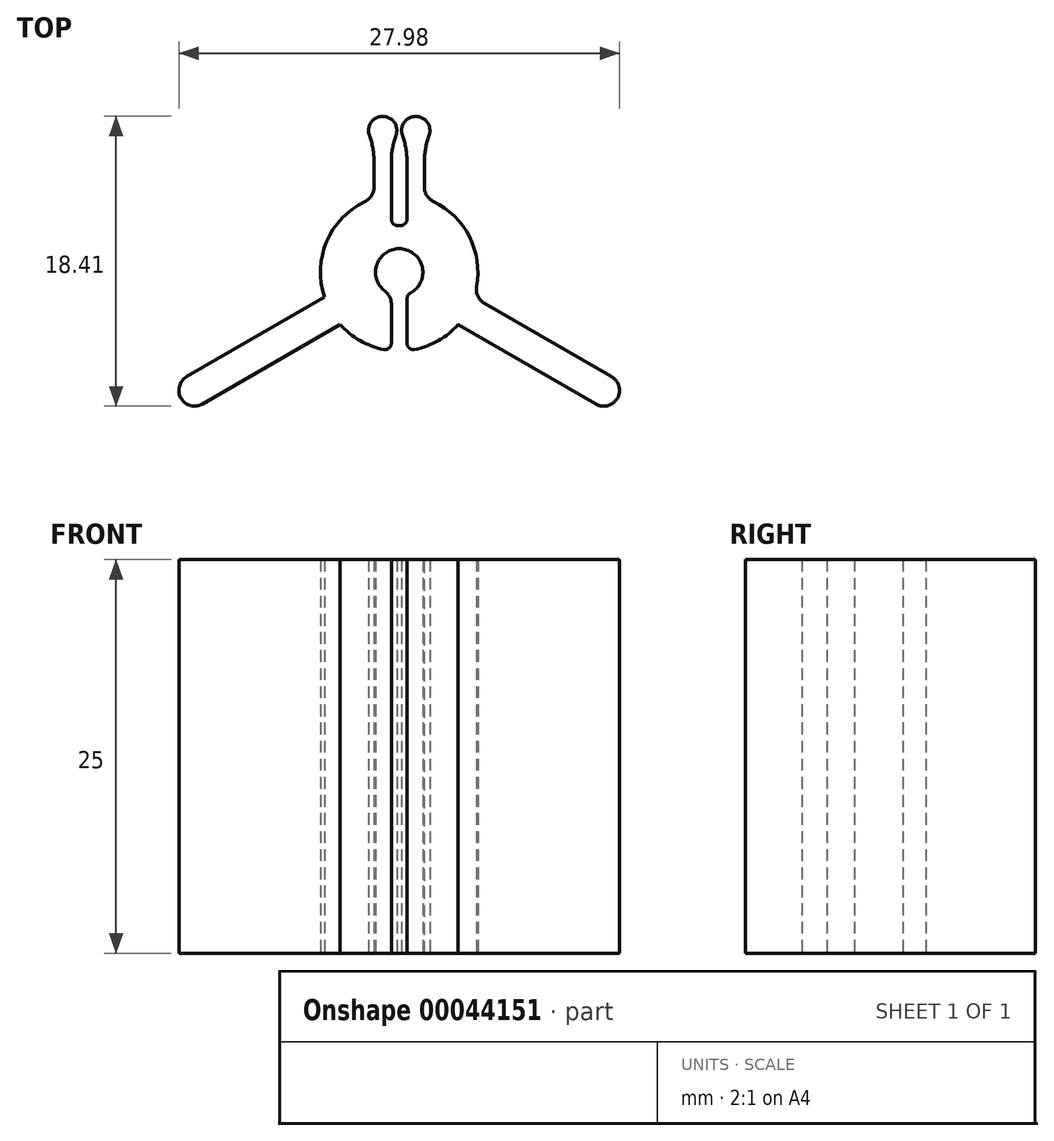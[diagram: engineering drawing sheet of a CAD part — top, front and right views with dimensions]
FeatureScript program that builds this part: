
annotation { "Feature Type Name" : "Feature", "Feature Type Description" : "" }
export const myFeature = defineFeature(function(context is Context, id is Id, definition is map)
    precondition{}
    {
        {
            var Q0;
            Q0=qCreatedBy(makeId("Top.planeOp"),FACE);
            var sketch = newSketch(context, id + "F0", { "sketchPlane" : qUnion([Q0])});
            skArc(sketch, "E0", {"start": v(-3.74, -3.32) * mm, "mid": v(-2.28, -4.45) * mm, "end": v(-0.5, -4.97) * mm});
            skArc(sketch, "E1", {"start": v(-0.5, 1.41) * mm, "mid": v(-1.5, 0) * mm, "end": v(-0.5, -1.41) * mm});
            skLineSegment(sketch, "E2", {"start": v(0, 0) * mm, "end": v(-44.7, -25.81) * mm, "construction": true});
            skLineSegment(sketch, "E3", {"start": v(0, 0) * mm, "end": v(14.9, -25.81) * mm, "construction": true});
            skLineSegment(sketch, "E4", {"start": v(-4.74, -1.58) * mm, "end": v(-13.5, -6.63) * mm});
            skLineSegment(sketch, "E5.MirrorCS", {"start": v(-3.74, -3.32) * mm, "end": v(-12.5, -8.37) * mm});
            skArc(sketch, "E6", {"start": v(-13.5, -6.63) * mm, "mid": v(-13.86, -8) * mm, "end": v(-12.5, -8.37) * mm});
            skPoint(sketch, "E7.orphan", {"position": v(-5.84, -2.21) * mm});
            skPoint(sketch, "E8.orphan", {"position": v(-4.84, -3.95) * mm});
            skLineSegment(sketch, "E9.MirrorCS", {"start": v(3.74, -3.32) * mm, "end": v(12.5, -8.37) * mm});
            skArc(sketch, "E10.MirrorCS", {"start": v(13.5, -6.63) * mm, "mid": v(13.86, -8) * mm, "end": v(12.5, -8.37) * mm});
            skLineSegment(sketch, "E11.MirrorCS", {"start": v(4.74, -1.58) * mm, "end": v(13.5, -6.63) * mm});
            skArc(sketch, "E12.trimOffspring", {"start": v(4.74, -1.58) * mm, "mid": v(4.48, 2.23) * mm, "end": v(1.6, 4.74) * mm});
            skLineSegment(sketch, "E13.MirrorCS", {"start": v(0.5, -4.97) * mm, "end": v(0.5, -1.41) * mm});
            skLineSegment(sketch, "E14.MirrorCS", {"start": v(-0.5, -4.97) * mm, "end": v(-0.5, -1.41) * mm});
            skArc(sketch, "E15.MirrorCS", {"start": v(-0.5, -1.41) * mm, "mid": v(0, 1.5) * mm, "end": v(0.5, -1.41) * mm});
            skArc(sketch, "E16.MirrorCS", {"start": v(-3.74, 3.32) * mm, "mid": v(-2.76, 4.17) * mm, "end": v(-1.6, 4.74) * mm});
            skArc(sketch, "E17.trimOffspring", {"start": v(0.5, -1.41) * mm, "mid": v(1.5, 0) * mm, "end": v(0.5, 1.41) * mm});
            skArc(sketch, "E18.trimOffspring", {"start": v(0.5, -4.97) * mm, "mid": v(2.28, -4.45) * mm, "end": v(3.74, -3.32) * mm});
            skLineSegment(sketch, "E19", {"start": v(-0.5, 4.37) * mm, "end": v(-0.5, 2.97) * mm});
            skLineSegment(sketch, "E20", {"start": v(-0.5, 2.97) * mm, "end": v(0, 2.97) * mm});
            skLineSegment(sketch, "E21.MirrorCS", {"start": v(0.5, 4.37) * mm, "end": v(0.5, 2.97) * mm});
            skLineSegment(sketch, "E22.MirrorCS", {"start": v(0.5, 2.97) * mm, "end": v(0, 2.97) * mm});
            skArc(sketch, "E23.trimOffspring", {"start": v(-3.74, 3.32) * mm, "mid": v(-4.9, 1) * mm, "end": v(-4.74, -1.58) * mm});
            skPoint(sketch, "E24.orphan", {"position": v(3.74, 3.32) * mm});
            skLineSegment(sketch, "E25", {"start": v(-1.6, 4.74) * mm, "end": v(-1.6, 8.3) * mm});
            skLineSegment(sketch, "E26", {"start": v(-0.5, 4.37) * mm, "end": v(-0.5, 8.3) * mm});
            skLineSegment(sketch, "E27.MirrorCS", {"start": v(0.5, 4.37) * mm, "end": v(0.5, 8.3) * mm});
            skLineSegment(sketch, "E28.MirrorCS", {"start": v(1.6, 4.74) * mm, "end": v(1.6, 8.3) * mm});
            skArc(sketch, "E29", {"start": v(-0.5, 8.3) * mm, "mid": v(-1.05, 9.9) * mm, "end": v(-1.6, 8.3) * mm});
            skPoint(sketch, "E30.orphan", {"position": v(-0.5, 9) * mm});
            skPoint(sketch, "E31.orphan", {"position": v(-1.6, 9) * mm});
            skArc(sketch, "E32.MirrorC", {"start": v(0.5, 8.3) * mm, "mid": v(1.05, 9.9) * mm, "end": v(1.6, 8.3) * mm});
            skPoint(sketch, "E33.orphan", {"position": v(0.5, 9) * mm});
            skPoint(sketch, "E34.MirrorCS.start.orphan", {"position": v(1.6, 9) * mm});
            skPoint(sketch, "E35.trimOffspring.end.orphan", {"position": v(0.5, 4.97) * mm});
            skPoint(sketch, "E36.trimOffspring.start.orphan", {"position": v(-0.5, 4.97) * mm});
            skSolve(sketch);
        }
        {
            var Q0;
            Q0 = qSketchRegion(id + "F0", true);
            extrude(context, id + "F1", {"entities" : qUnion([Q0]), "depth" : 25 * mm, "offsetDistance" : 25 * mm});
        }
        {
            var Q0;
            Q0=makeQuery(id+"F1.opExtrude","SWEPT_EDGE",EDGE,{"disambiguationData":[OSD([sQuery(id+"F0.wireOp",EDGE,"3mzkk0lv-jN8c-HgQ4-SjRx-xyB0a0JVrphj"),sQuery(id+"F0.wireOp",EDGE,"E36.trimOffspring")])]});
            var Q1;
            Q1=makeQuery(id+"F1.opExtrude","SWEPT_EDGE",EDGE,{"disambiguationData":[OSD([sQuery(id+"F0.wireOp",EDGE,"E12.trimOffspring"),sQuery(id+"F0.wireOp",EDGE,"587d526e-da83-4a6c-8857-2415be24daab0.MirrorCS")])]});
            var Q2;
            Q2=makeQuery(id+"F1.opExtrude","SWEPT_EDGE",EDGE,{"disambiguationData":[OSD([sQuery(id+"F0.wireOp",EDGE,"E1"),sQuery(id+"F0.wireOp",EDGE,"3mzkk0lv-jN8c-HgQ4-SjRx-xyB0a0JVrphj")])]});
            var Q3;
            Q3=makeQuery(id+"F1.opExtrude","SWEPT_EDGE",EDGE,{"disambiguationData":[OSD([sQuery(id+"F0.wireOp",EDGE,"E1"),sQuery(id+"F0.wireOp",EDGE,"587d526e-da83-4a6c-8857-2415be24daab0.MirrorCS")])]});
            var Q4;
            Q4=makeQuery(id+"F1.opExtrude","SWEPT_EDGE",EDGE,{"disambiguationData":[OSD([sQuery(id+"F0.wireOp",EDGE,"E16.MirrorCS"),sQuery(id+"F0.wireOp",EDGE,"E25")])]});
            fillet(context, id + "F2", {"entities" : qUnion([Q0, Q1, Q2, Q3, Q4]), "radius" : 1 * mm, "tangentPropagation" : true, "allowEdgeOverflow" : false});
        }
        {
            var Q0;
            Q0=makeQuery(id+"F1.opExtrude","SWEPT_EDGE",EDGE,{"disambiguationData":[OSD([sQuery(id+"F0.wireOp",EDGE,"E19"),sQuery(id+"F0.wireOp",EDGE,"E20")])]});
            var Q1;
            Q1=makeQuery(id+"F1.opExtrude","SWEPT_EDGE",EDGE,{"disambiguationData":[OSD([sQuery(id+"F0.wireOp",EDGE,"E21.MirrorCS"),sQuery(id+"F0.wireOp",EDGE,"E22.MirrorCS")])]});
            var Q2;
            Q2=makeQuery(id+"F1.opExtrude","SWEPT_EDGE",EDGE,{"disambiguationData":[OSD([sQuery(id+"F0.wireOp",EDGE,"E21.MirrorCS"),sQuery(id+"F0.wireOp",EDGE,"d01798ca-214c-46cb-be73-290c21217de8.trimOffspring")])]});
            var Q3;
            Q3=makeQuery(id+"F1.opExtrude","SWEPT_EDGE",EDGE,{"disambiguationData":[OSD([sQuery(id+"F0.wireOp",EDGE,"E16.MirrorCS"),sQuery(id+"F0.wireOp",EDGE,"E19")])]});
            var Q4;
            Q4=makeQuery(id+"F1.opExtrude","SWEPT_EDGE",EDGE,{"disambiguationData":[OSD([sQuery(id+"F0.wireOp",EDGE,"E13.MirrorCS"),sQuery(id+"F0.wireOp",EDGE,"E17.trimOffspring")])]});
            var Q5;
            Q5=makeQuery(id+"F1.opExtrude","SWEPT_EDGE",EDGE,{"disambiguationData":[OSD([sQuery(id+"F0.wireOp",EDGE,"E14.MirrorCS"),sQuery(id+"F0.wireOp",EDGE,"E15.MirrorCS")])]});
            var Q6;
            Q6=makeQuery(id+"F1.opExtrude","SWEPT_EDGE",EDGE,{"disambiguationData":[OSD([sQuery(id+"F0.wireOp",EDGE,"E13.MirrorCS"),sQuery(id+"F0.wireOp",EDGE,"E18.trimOffspring")])]});
            var Q7;
            Q7=makeQuery(id+"F1.opExtrude","SWEPT_EDGE",EDGE,{"disambiguationData":[OSD([sQuery(id+"F0.wireOp",EDGE,"E0"),sQuery(id+"F0.wireOp",EDGE,"E14.MirrorCS")])]});
            fillet(context, id + "F3", {"entities" : qUnion([Q0, Q1, Q2, Q3, Q4, Q5, Q6, Q7]), "radius" : .4 * mm, "tangentPropagation" : true, "allowEdgeOverflow" : false});
        }
        {
            var Q0;
            Q0=makeQuery(id+"F1.opExtrude","SWEPT_EDGE",EDGE,{"disambiguationData":[OSD([sQuery(id+"F0.wireOp",EDGE,"E25"),sQuery(id+"F0.wireOp",EDGE,"E29")])]});
            var Q1;
            Q1=makeQuery(id+"F1.opExtrude","SWEPT_EDGE",EDGE,{"disambiguationData":[OSD([sQuery(id+"F0.wireOp",EDGE,"E26"),sQuery(id+"F0.wireOp",EDGE,"E29")])]});
            var Q2;
            Q2=makeQuery(id+"F1.opExtrude","SWEPT_EDGE",EDGE,{"disambiguationData":[OSD([sQuery(id+"F0.wireOp",EDGE,"E28.MirrorCS"),sQuery(id+"F0.wireOp",EDGE,"E32.MirrorC")])]});
            var Q3;
            Q3=makeQuery(id+"F1.opExtrude","SWEPT_EDGE",EDGE,{"disambiguationData":[OSD([sQuery(id+"F0.wireOp",EDGE,"E27.MirrorCS"),sQuery(id+"F0.wireOp",EDGE,"E32.MirrorC")])]});
            fillet(context, id + "F4", {"entities" : qUnion([Q0, Q1, Q2, Q3]), "radius" : 5 * mm, "tangentPropagation" : true, "allowEdgeOverflow" : false});
        }
    });
